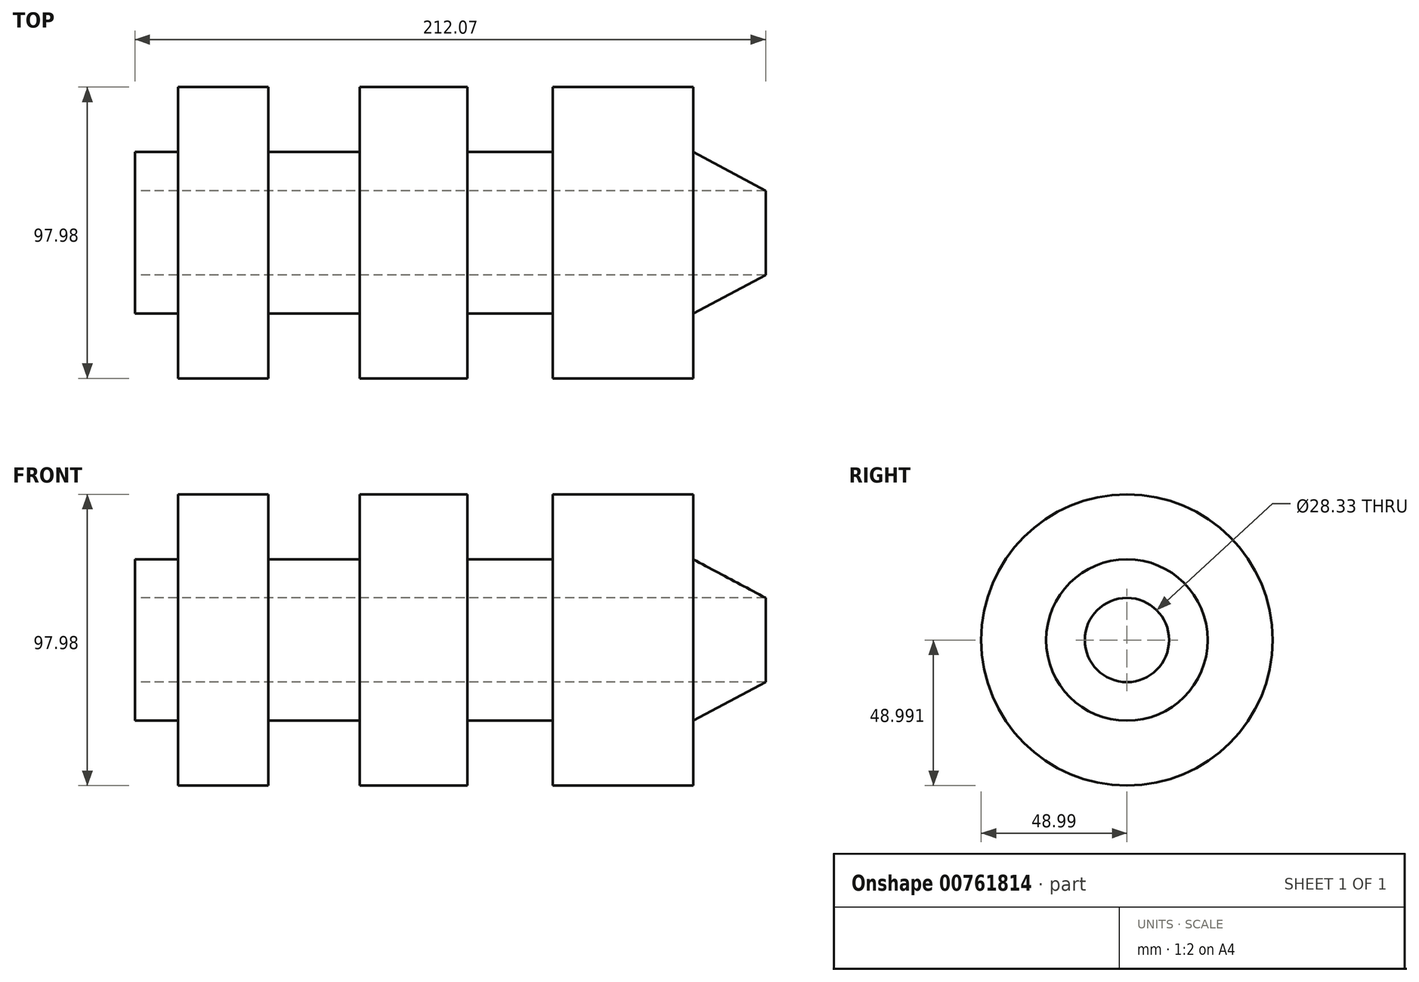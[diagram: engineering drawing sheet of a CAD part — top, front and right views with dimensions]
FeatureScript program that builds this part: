
annotation { "Feature Type Name" : "Feature", "Feature Type Description" : "" }
export const myFeature = defineFeature(function(context is Context, id is Id, definition is map)
    precondition{}
    {
        {
            var Q0;
            Q0=qCreatedBy(makeId("Front.planeOp"),FACE);
            var sketch = newSketch(context, id + "F0", { "sketchPlane" : qUnion([Q0])});
            skLineSegment(sketch, "E0", {"start": v(-97.38, -34.82) * mm, "end": v(114.7, -34.82) * mm});
            skLineSegment(sketch, "E1", {"start": v(114.7, -34.82) * mm, "end": v(90.3, -21.84) * mm});
            skLineSegment(sketch, "E2", {"start": v(90.3, -21.84) * mm, "end": v(90.3, 0) * mm});
            skLineSegment(sketch, "E3", {"start": v(90.3, 0) * mm, "end": v(43.08, 0) * mm});
            skLineSegment(sketch, "E4", {"start": v(43.08, 0) * mm, "end": v(43.08, -21.84) * mm});
            skLineSegment(sketch, "E5", {"start": v(43.08, -21.84) * mm, "end": v(14.36, -21.84) * mm});
            skPoint(sketch, "E6.end.orphan", {"position": v(14.36, 0) * mm});
            skLineSegment(sketch, "E7", {"start": v(14.36, 0) * mm, "end": v(14.36, -21.84) * mm});
            skLineSegment(sketch, "E8", {"start": v(14.36, 0) * mm, "end": v(-21.84, 0) * mm});
            skLineSegment(sketch, "E9", {"start": v(-21.84, 0) * mm, "end": v(-21.84, -21.84) * mm});
            skLineSegment(sketch, "E10", {"start": v(-21.84, -21.84) * mm, "end": v(-52.53, -21.84) * mm});
            skLineSegment(sketch, "E11", {"start": v(-52.53, -21.84) * mm, "end": v(-52.53, 0) * mm});
            skLineSegment(sketch, "E12", {"start": v(-52.53, 0) * mm, "end": v(-82.82, 0) * mm});
            skLineSegment(sketch, "E13", {"start": v(-82.82, 0) * mm, "end": v(-82.82, -21.84) * mm});
            skLineSegment(sketch, "E14", {"start": v(-82.82, -21.84) * mm, "end": v(-97.38, -21.84) * mm});
            skLineSegment(sketch, "E15", {"start": v(-97.38, -21.84) * mm, "end": v(-97.38, -34.82) * mm});
            skLineSegment(sketch, "E16", {"start": v(-102.5, -48.99) * mm, "end": v(115.48, -48.99) * mm, "construction": true});
            skSolve(sketch);
        }
        {
            var Q0;
            Q0=makeQuery(id+"F0.imprint","IMPRINT",FACE,{"disambiguationData":[TD([[makeQuery(id+"F0.imprint","IMPRINT",EDGE,{"derivedFrom":sQuery(id+"F0.wireOp",EDGE,"E0")}),1.0]])]});
            var Q1;
            Q1=sQuery(id+"F0.wireOp",EDGE,"E16");
            revolve(context, id + "F1", {"surfaceOperationType" : NewSurfaceOperationType.NEW, "entities" : qUnion([Q0]), "axis" : qUnion([Q1]), "revolveType" : RevolveType.FULL});
        }
    });
